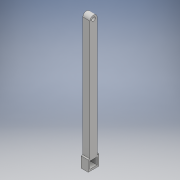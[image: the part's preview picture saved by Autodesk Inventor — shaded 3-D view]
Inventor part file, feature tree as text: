
AUTODESK INVENTOR PART (.ipt)
format: ipt  version: 2018 (Build 220112000, 112)  size: 111,616 bytes
history: native  units: mm
features: extrude x1, sketch x1
ambient origin geometry x8: Origin, YZ Plane, XZ Plane, XY Plane, X Axis, Y Axis, Z Axis, Center Point
bodies: Solid1 (feature_tree)
feature tree (2):
  extrude  "Extrusion1"  Depth=20.0mm
  sketch  "Sketch1"  dims[d4=40.0mm d5=20.0mm d6=40.0mm d7=40.0mm d8=60.0mm d9=60.0mm d11=10.0mm d13=20.0mm d14=40.0mm d15=0.0mm]
